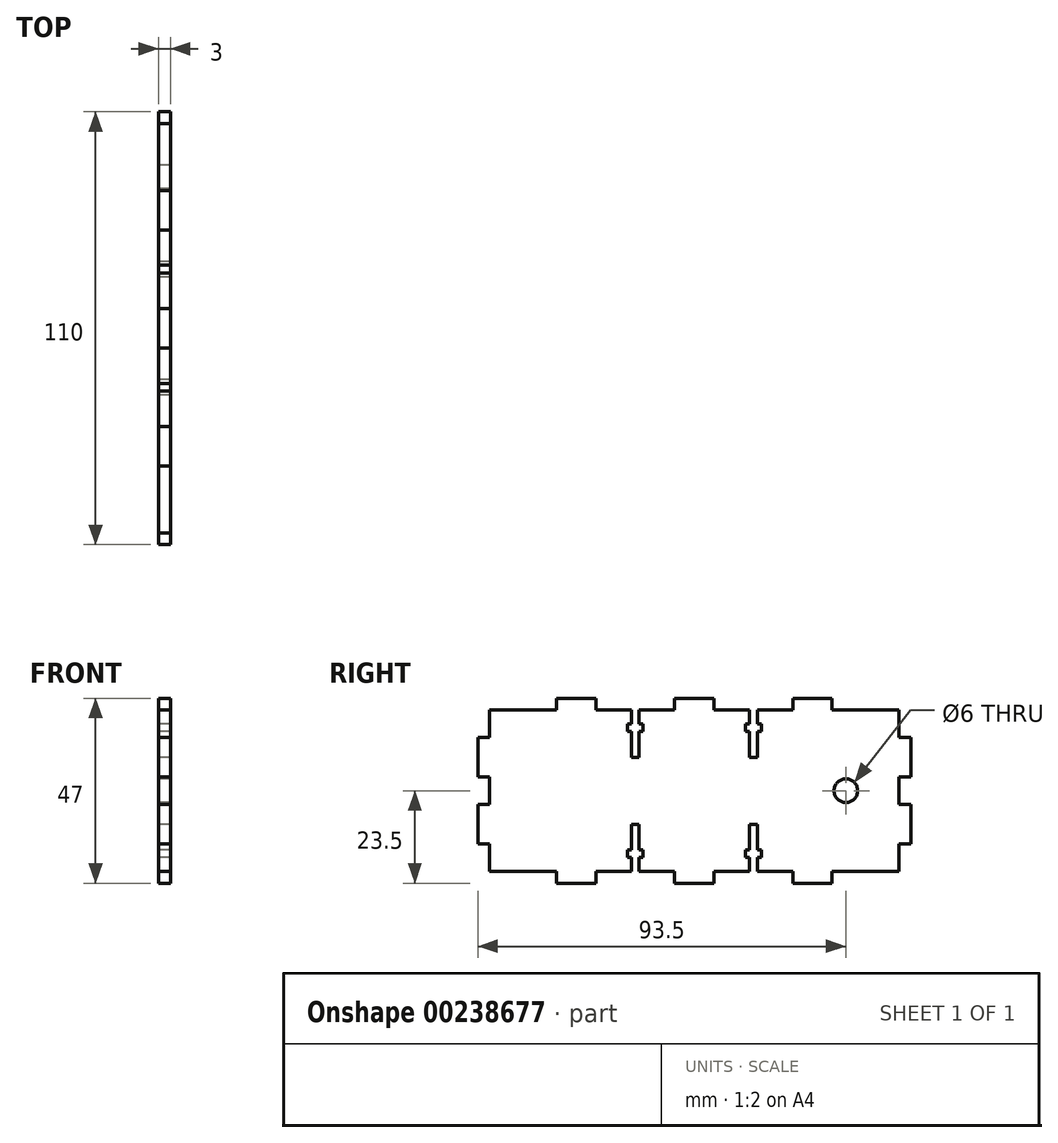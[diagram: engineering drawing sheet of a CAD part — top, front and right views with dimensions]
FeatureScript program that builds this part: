
annotation { "Feature Type Name" : "Feature", "Feature Type Description" : "" }
export const myFeature = defineFeature(function(context is Context, id is Id, definition is map)
    precondition{}
    {
        {
            var Q0;
            Q0=qCreatedBy(makeId("Right.planeOp"),FACE);
            var sketch = newSketch(context, id + "F0", { "sketchPlane" : qUnion([Q0])});
            skLineSegment(sketch, "E0", {"start": v(0, 0) * mm, "end": v(0, 7) * mm});
            skLineSegment(sketch, "E1", {"start": v(0, 7) * mm, "end": v(-3, 7) * mm});
            skLineSegment(sketch, "E2", {"start": v(-3, 7) * mm, "end": v(-3, 17) * mm});
            skLineSegment(sketch, "E3", {"start": v(-3, 17) * mm, "end": v(0, 17) * mm});
            skLineSegment(sketch, "E4", {"start": v(0, 17) * mm, "end": v(0, 20.5) * mm});
            skLineSegment(sketch, "E5", {"start": v(0, 0) * mm, "end": v(17, 0) * mm});
            skLineSegment(sketch, "E6", {"start": v(17, 0) * mm, "end": v(17, -3) * mm});
            skLineSegment(sketch, "E7", {"start": v(17, -3) * mm, "end": v(27, -3) * mm});
            skLineSegment(sketch, "E8", {"start": v(27, 0) * mm, "end": v(27, -3) * mm});
            skLineSegment(sketch, "E9", {"start": v(27, 0) * mm, "end": v(36, 0) * mm});
            skLineSegment(sketch, "E10", {"start": v(36, 0) * mm, "end": v(36, 3.5) * mm});
            skLineSegment(sketch, "E11", {"start": v(36, 3.5) * mm, "end": v(35, 3.5) * mm});
            skLineSegment(sketch, "E12", {"start": v(35, 3.5) * mm, "end": v(35, 5.5) * mm});
            skLineSegment(sketch, "E13", {"start": v(35, 5.5) * mm, "end": v(36, 5.5) * mm});
            skLineSegment(sketch, "E14", {"start": v(36, 5.5) * mm, "end": v(36, 12) * mm});
            skLineSegment(sketch, "E15", {"start": v(36, 12) * mm, "end": v(38, 12) * mm});
            skLineSegment(sketch, "E16", {"start": v(38, 12) * mm, "end": v(38, 5.5) * mm});
            skLineSegment(sketch, "E17", {"start": v(38, 5.5) * mm, "end": v(39, 5.5) * mm});
            skLineSegment(sketch, "E18", {"start": v(38, 3.5) * mm, "end": v(39, 3.5) * mm});
            skLineSegment(sketch, "E19", {"start": v(38, 0) * mm, "end": v(38, 3.5) * mm});
            skLineSegment(sketch, "E20", {"start": v(38, 0) * mm, "end": v(47, 0) * mm});
            skLineSegment(sketch, "E21", {"start": v(39, 3.5) * mm, "end": v(39, 5.5) * mm});
            skLineSegment(sketch, "E22", {"start": v(47, 0) * mm, "end": v(47, -3) * mm});
            skLineSegment(sketch, "E23", {"start": v(47, -3) * mm, "end": v(52, -3) * mm});
            skLineSegment(sketch, "E24", {"start": v(0, 20.5) * mm, "end": v(52, 20.5) * mm, "construction": true});
            skLineSegment(sketch, "E25", {"start": v(52, 20.5) * mm, "end": v(52, -3) * mm, "construction": true});
            skLineSegment(sketch, "E26.MirrorCS", {"start": v(35, 35.5) * mm, "end": v(36, 35.5) * mm});
            skLineSegment(sketch, "E27.MirrorCS", {"start": v(39, 37.5) * mm, "end": v(39, 35.5) * mm});
            skLineSegment(sketch, "E28.MirrorCS", {"start": v(36, 37.5) * mm, "end": v(35, 37.5) * mm});
            skLineSegment(sketch, "E29.MirrorCS", {"start": v(35, 37.5) * mm, "end": v(35, 35.5) * mm});
            skLineSegment(sketch, "E30.MirrorCS", {"start": v(38, 35.5) * mm, "end": v(39, 35.5) * mm});
            skLineSegment(sketch, "E31.MirrorCS", {"start": v(38, 37.5) * mm, "end": v(39, 37.5) * mm});
            skLineSegment(sketch, "E32.MirrorCS", {"start": v(36, 29) * mm, "end": v(38, 29) * mm});
            skLineSegment(sketch, "E33.MirrorCS", {"start": v(36, 41) * mm, "end": v(36, 37.5) * mm});
            skLineSegment(sketch, "E34.MirrorCS", {"start": v(27, 41) * mm, "end": v(27, 44) * mm});
            skLineSegment(sketch, "E35.MirrorCS", {"start": v(0, 34) * mm, "end": v(-3, 34) * mm});
            skLineSegment(sketch, "E36.MirrorCS", {"start": v(36, 35.5) * mm, "end": v(36, 29) * mm});
            skLineSegment(sketch, "E37.MirrorCS", {"start": v(38, 41) * mm, "end": v(38, 37.5) * mm});
            skLineSegment(sketch, "E38.MirrorCS", {"start": v(27, 41) * mm, "end": v(36, 41) * mm});
            skLineSegment(sketch, "E39.MirrorCS", {"start": v(38, 29) * mm, "end": v(38, 35.5) * mm});
            skLineSegment(sketch, "E40.MirrorCS", {"start": v(38, 41) * mm, "end": v(47, 41) * mm});
            skLineSegment(sketch, "E41.MirrorCS", {"start": v(0, 41) * mm, "end": v(17, 41) * mm});
            skLineSegment(sketch, "E42.MirrorCS", {"start": v(17, 41) * mm, "end": v(17, 44) * mm});
            skLineSegment(sketch, "E43.MirrorCS", {"start": v(-3, 34) * mm, "end": v(-3, 24) * mm});
            skLineSegment(sketch, "E44.MirrorCS", {"start": v(-3, 24) * mm, "end": v(0, 24) * mm});
            skLineSegment(sketch, "E45.MirrorCS", {"start": v(0, 41) * mm, "end": v(0, 34) * mm});
            skLineSegment(sketch, "E46.MirrorCS", {"start": v(47, 41) * mm, "end": v(47, 44) * mm});
            skLineSegment(sketch, "E47.MirrorCS", {"start": v(17, 44) * mm, "end": v(27, 44) * mm});
            skLineSegment(sketch, "E48.MirrorCS", {"start": v(0, 24) * mm, "end": v(0, 20.5) * mm});
            skLineSegment(sketch, "E49.MirrorCS", {"start": v(47, 44) * mm, "end": v(52, 44) * mm});
            skLineSegment(sketch, "E50.MirrorCS", {"start": v(52, 20.5) * mm, "end": v(52, 44) * mm, "construction": true});
            skLineSegment(sketch, "E51.MirrorCS", {"start": v(69, 37.5) * mm, "end": v(69, 35.5) * mm});
            skLineSegment(sketch, "E52.MirrorCS", {"start": v(69, 35.5) * mm, "end": v(68, 35.5) * mm});
            skLineSegment(sketch, "E53.MirrorCS", {"start": v(68, 29) * mm, "end": v(66, 29) * mm});
            skLineSegment(sketch, "E54.MirrorCS", {"start": v(66, 37.5) * mm, "end": v(65, 37.5) * mm});
            skLineSegment(sketch, "E55.MirrorCS", {"start": v(66, 3.5) * mm, "end": v(65, 3.5) * mm});
            skLineSegment(sketch, "E56.MirrorCS", {"start": v(68, 3.5) * mm, "end": v(69, 3.5) * mm});
            skLineSegment(sketch, "E57.MirrorCS", {"start": v(69, 3.5) * mm, "end": v(69, 5.5) * mm});
            skLineSegment(sketch, "E58.MirrorCS", {"start": v(66, 5.5) * mm, "end": v(65, 5.5) * mm});
            skLineSegment(sketch, "E59.MirrorCS", {"start": v(65, 37.5) * mm, "end": v(65, 35.5) * mm});
            skLineSegment(sketch, "E60.MirrorCS", {"start": v(66, 35.5) * mm, "end": v(65, 35.5) * mm});
            skLineSegment(sketch, "E61.MirrorCS", {"start": v(69, 5.5) * mm, "end": v(68, 5.5) * mm});
            skLineSegment(sketch, "E62.MirrorCS", {"start": v(65, 3.5) * mm, "end": v(65, 5.5) * mm});
            skLineSegment(sketch, "E63.MirrorCS", {"start": v(68, 37.5) * mm, "end": v(69, 37.5) * mm});
            skLineSegment(sketch, "E64.MirrorCS", {"start": v(68, 12) * mm, "end": v(66, 12) * mm});
            skLineSegment(sketch, "E65.MirrorCS", {"start": v(77, 41) * mm, "end": v(77, 44) * mm});
            skLineSegment(sketch, "E66.MirrorCS", {"start": v(66, 0) * mm, "end": v(57, 0) * mm});
            skLineSegment(sketch, "E67.MirrorCS", {"start": v(104, 41) * mm, "end": v(104, 34) * mm});
            skLineSegment(sketch, "E68.MirrorCS", {"start": v(87, 41) * mm, "end": v(87, 44) * mm});
            skLineSegment(sketch, "E69.MirrorCS", {"start": v(66, 0) * mm, "end": v(66, 3.5) * mm});
            skLineSegment(sketch, "E70.MirrorCS", {"start": v(66, 12) * mm, "end": v(66, 5.5) * mm});
            skLineSegment(sketch, "E71.MirrorCS", {"start": v(68, 35.5) * mm, "end": v(68, 29) * mm});
            skLineSegment(sketch, "E72.MirrorCS", {"start": v(104, 24) * mm, "end": v(104, 20.5) * mm});
            skLineSegment(sketch, "E73.MirrorCS", {"start": v(104, 34) * mm, "end": v(107, 34) * mm});
            skLineSegment(sketch, "E74.MirrorCS", {"start": v(87, 44) * mm, "end": v(77, 44) * mm});
            skLineSegment(sketch, "E75.MirrorCS", {"start": v(68, 0) * mm, "end": v(68, 3.5) * mm});
            skLineSegment(sketch, "E76.MirrorCS", {"start": v(68, 41) * mm, "end": v(68, 37.5) * mm});
            skLineSegment(sketch, "E77.MirrorCS", {"start": v(87, 0) * mm, "end": v(87, -3) * mm});
            skLineSegment(sketch, "E78.MirrorCS", {"start": v(104, 0) * mm, "end": v(104, 7) * mm});
            skLineSegment(sketch, "E79.MirrorCS", {"start": v(57, 44) * mm, "end": v(52, 44) * mm});
            skLineSegment(sketch, "E80.MirrorCS", {"start": v(77, 0) * mm, "end": v(68, 0) * mm});
            skLineSegment(sketch, "E81.MirrorCS", {"start": v(57, 0) * mm, "end": v(57, -3) * mm});
            skLineSegment(sketch, "E82.MirrorCS", {"start": v(104, 7) * mm, "end": v(107, 7) * mm});
            skLineSegment(sketch, "E83.MirrorCS", {"start": v(77, 41) * mm, "end": v(68, 41) * mm});
            skLineSegment(sketch, "E84.MirrorCS", {"start": v(107, 34) * mm, "end": v(107, 24) * mm});
            skLineSegment(sketch, "E85.MirrorCS", {"start": v(107, 7) * mm, "end": v(107, 17) * mm});
            skLineSegment(sketch, "E86.MirrorCS", {"start": v(66, 29) * mm, "end": v(66, 35.5) * mm});
            skLineSegment(sketch, "E87.MirrorCS", {"start": v(57, -3) * mm, "end": v(52, -3) * mm});
            skLineSegment(sketch, "E88.MirrorCS", {"start": v(66, 41) * mm, "end": v(66, 37.5) * mm});
            skLineSegment(sketch, "E89.MirrorCS", {"start": v(57, 41) * mm, "end": v(57, 44) * mm});
            skLineSegment(sketch, "E90.MirrorCS", {"start": v(66, 41) * mm, "end": v(57, 41) * mm});
            skLineSegment(sketch, "E91.MirrorCS", {"start": v(104, 20.5) * mm, "end": v(52, 20.5) * mm, "construction": true});
            skLineSegment(sketch, "E92.MirrorCS", {"start": v(107, 24) * mm, "end": v(104, 24) * mm});
            skLineSegment(sketch, "E93.MirrorCS", {"start": v(104, 0) * mm, "end": v(87, 0) * mm});
            skLineSegment(sketch, "E94.MirrorCS", {"start": v(87, -3) * mm, "end": v(77, -3) * mm});
            skLineSegment(sketch, "E95.MirrorCS", {"start": v(68, 5.5) * mm, "end": v(68, 12) * mm});
            skLineSegment(sketch, "E96.MirrorCS", {"start": v(77, 0) * mm, "end": v(77, -3) * mm});
            skLineSegment(sketch, "E97.MirrorCS", {"start": v(104, 41) * mm, "end": v(87, 41) * mm});
            skLineSegment(sketch, "E98.MirrorCS", {"start": v(104, 17) * mm, "end": v(104, 20.5) * mm});
            skLineSegment(sketch, "E99.MirrorCS", {"start": v(107, 17) * mm, "end": v(104, 17) * mm});
            skCircle(sketch, "E100", {"center": v(90.5, 20.5) * mm, "radius": 3 * mm});
            skSolve(sketch);
        }
        {
            var Q0;
            Q0=qSketchRegion(id+"F0",true);
            extrude(context, id + "F1", {"entities" : qUnion([Q0]), "depth" : 3 * mm});
        }
    });
